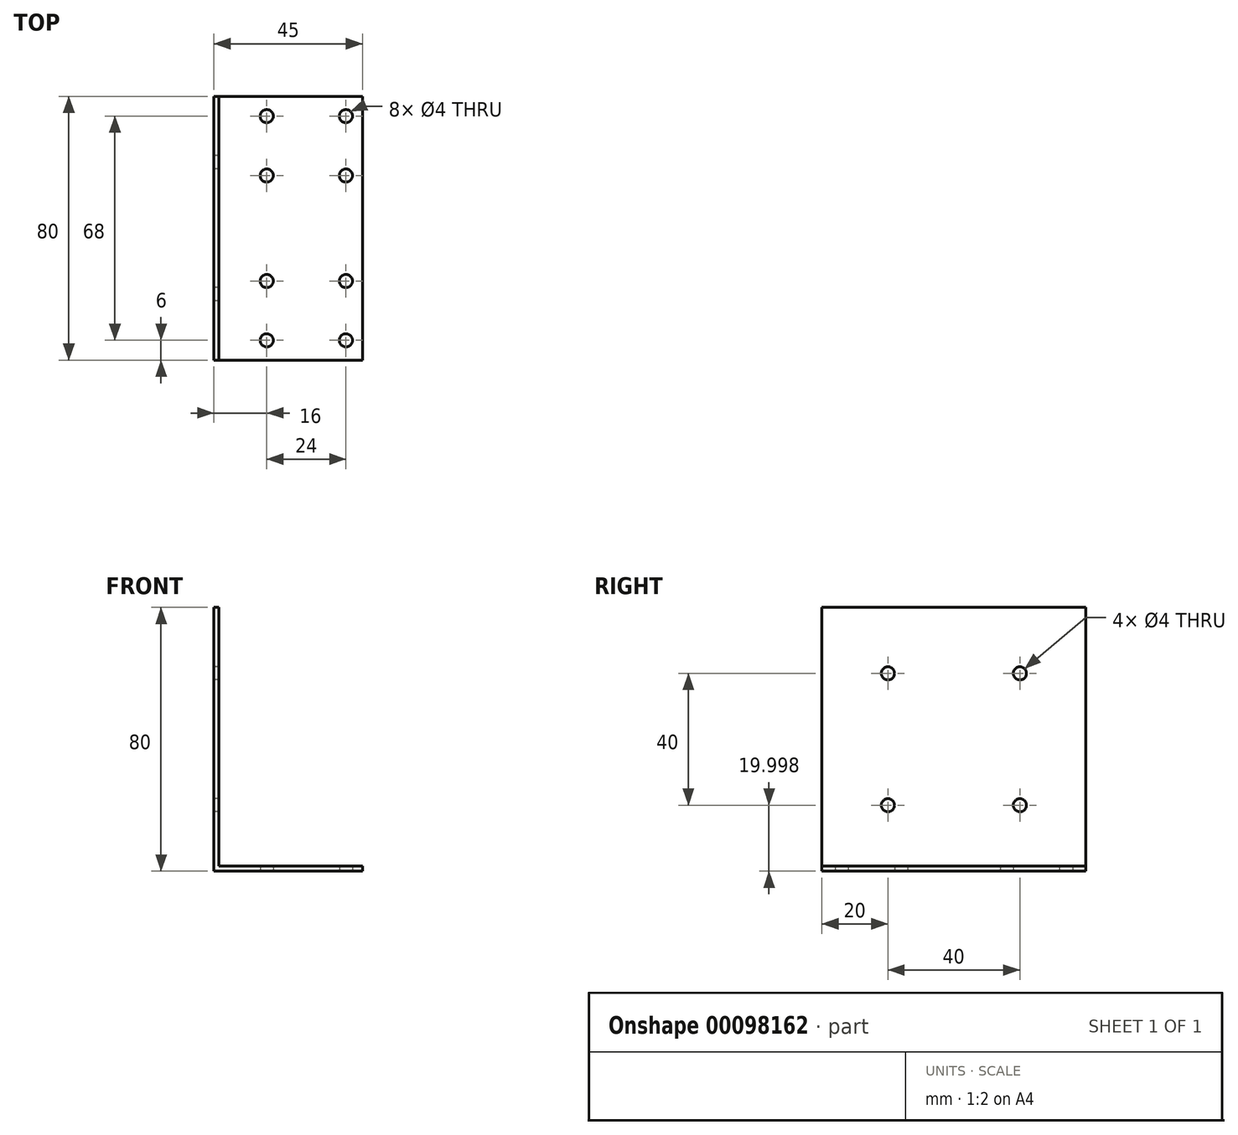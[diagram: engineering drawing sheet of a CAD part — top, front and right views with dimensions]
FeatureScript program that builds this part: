
annotation { "Feature Type Name" : "Feature", "Feature Type Description" : "" }
export const myFeature = defineFeature(function(context is Context, id is Id, definition is map)
    precondition{}
    {
        {
            var Q0;
            Q0=qCreatedBy(makeId("Front.planeOp"),FACE);
            var sketch = newSketch(context, id + "F0", { "sketchPlane" : qUnion([Q0])});
            skLineSegment(sketch, "E0", {"start": v(-85.27, 112.48) * mm, "end": v(-85.27, 32.48) * mm});
            skLineSegment(sketch, "E1", {"start": v(-85.27, 32.48) * mm, "end": v(-40.27, 32.48) * mm});
            skLineSegment(sketch, "E2", {"start": v(-40.27, 32.48) * mm, "end": v(-40.27, 33.98) * mm});
            skLineSegment(sketch, "E3", {"start": v(-40.27, 33.98) * mm, "end": v(-83.77, 33.98) * mm});
            skLineSegment(sketch, "E4", {"start": v(-83.77, 33.98) * mm, "end": v(-83.77, 112.48) * mm});
            skLineSegment(sketch, "E5", {"start": v(-83.77, 112.48) * mm, "end": v(-85.27, 112.48) * mm});
            skSolve(sketch);
        }
        {
            var Q0;
            Q0=makeQuery(id+"F0.imprint","IMPRINT",FACE,{"disambiguationData":[TD([[makeQuery(id+"F0.imprint","IMPRINT",EDGE,{"derivedFrom":sQuery(id+"F0.wireOp",EDGE,"E0")}),1.0]])]});
            extrude(context, id + "F1", {"entities" : qUnion([Q0]), "depth" : 80 * mm});
        }
        {
            var Q0;
            Q0=makeQuery(id+"F1.opExtrude","SWEPT_FACE",FACE,{"disambiguationData":[OSD([sQuery(id+"F0.wireOp",EDGE,"E1")])]});
            var sketch = newSketch(context, id + "F2", { "sketchPlane" : qUnion([Q0])});
            skPoint(sketch, "E6.startSnap0", {"position": v(-62.77, 80) * mm});
            skLineSegment(sketch, "E7", {"start": v(-94.66, 40) * mm, "end": v(-37.45, 40) * mm, "construction": true});
            skPoint(sketch, "E7.startSnap0", {"position": v(-85.27, 40) * mm});
            skLineSegment(sketch, "E8", {"start": v(-91.67, 65) * mm, "end": v(-32.26, 65) * mm, "construction": true});
            skPoint(sketch, "E9.MirrorP", {"position": v(-45.27, 74) * mm});
            skLineSegment(sketch, "E10", {"start": v(-57.27, -6.03) * mm, "end": v(-57.27, 93.49) * mm, "construction": true});
            skPoint(sketch, "E11.MirrorP", {"position": v(-45.27, 56) * mm});
            skPoint(sketch, "E12.MirrorP", {"position": v(-69.27, 56) * mm});
            skPoint(sketch, "E13.MirrorP", {"position": v(-69.27, 74) * mm});
            skPoint(sketch, "E14.MirrorP", {"position": v(-69.27, 24) * mm});
            skPoint(sketch, "E15.MirrorP", {"position": v(-69.27, 6) * mm});
            skPoint(sketch, "E16.MirrorP", {"position": v(-45.27, 6) * mm});
            skPoint(sketch, "E17.MirrorP", {"position": v(-45.27, 24) * mm});
            skSolve(sketch);
        }
        {
            var Q0;
            Q0=sQuery(id+"F2.wireOp",VERTEX,"E9.MirrorP");
            var Q1;
            Q1=sQuery(id+"F2.wireOp",VERTEX,"E13.MirrorP");
            var Q2;
            Q2=sQuery(id+"F2.wireOp",VERTEX,"E12.MirrorP");
            var Q3;
            Q3=sQuery(id+"F2.wireOp",VERTEX,"E11.MirrorP");
            var Q4;
            Q4=sQuery(id+"F2.wireOp",VERTEX,"E17.MirrorP");
            var Q5;
            Q5=sQuery(id+"F2.wireOp",VERTEX,"E16.MirrorP");
            var Q6;
            Q6=sQuery(id+"F2.wireOp",VERTEX,"E15.MirrorP");
            var Q7;
            Q7=sQuery(id+"F2.wireOp",VERTEX,"E14.MirrorP");
            var Q8;
            Q8=makeQuery(id+"F1.opExtrude","SWEPT_BODY",BODY,{"disambiguationData":[OSD([sQuery(id+"F0.wireOp",EDGE,"E0"),sQuery(id+"F0.wireOp",EDGE,"E1"),sQuery(id+"F0.wireOp",EDGE,"E2"),sQuery(id+"F0.wireOp",EDGE,"E3"),sQuery(id+"F0.wireOp",EDGE,"E4"),sQuery(id+"F0.wireOp",EDGE,"E5")])]});
            hole(context, id + "F3", {"style" : HoleStyle.SIMPLE, "endStyle" : HoleEndStyle.THROUGH, "holeDiameter" : 4 * mm, "locations" : qUnion([Q0, Q1, Q2, Q3, Q4, Q5, Q6, Q7]), "scope" : qUnion([Q8]), "isTappedThrough" : true});
        }
        {
            var Q0;
            Q0=makeQuery(id+"F1.opExtrude","SWEPT_FACE",FACE,{"disambiguationData":[OSD([sQuery(id+"F0.wireOp",EDGE,"E0")])]});
            var sketch = newSketch(context, id + "F4", { "sketchPlane" : qUnion([Q0])});
            skPoint(sketch, "E18", {"position": v(20, 92.48) * mm});
            skPoint(sketch, "E19", {"position": v(20, 52.48) * mm});
            skPoint(sketch, "E20", {"position": v(60, 52.48) * mm});
            skPoint(sketch, "E21", {"position": v(60, 92.48) * mm});
            skSolve(sketch);
        }
        {
            var Q0;
            Q0=sQuery(id+"F4.wireOp",VERTEX,"E19");
            var Q1;
            Q1=sQuery(id+"F4.wireOp",VERTEX,"E20");
            var Q2;
            Q2=sQuery(id+"F4.wireOp",VERTEX,"E21");
            var Q3;
            Q3=sQuery(id+"F4.wireOp",VERTEX,"E18");
            var Q4;
            Q4=makeQuery(id+"F1.opExtrude","SWEPT_BODY",BODY,{"disambiguationData":[OSD([sQuery(id+"F0.wireOp",EDGE,"E0"),sQuery(id+"F0.wireOp",EDGE,"E1"),sQuery(id+"F0.wireOp",EDGE,"E2"),sQuery(id+"F0.wireOp",EDGE,"E3"),sQuery(id+"F0.wireOp",EDGE,"E4"),sQuery(id+"F0.wireOp",EDGE,"E5")])]});
            hole(context, id + "F5", {"style" : HoleStyle.SIMPLE, "endStyle" : HoleEndStyle.THROUGH, "holeDiameter" : 4 * mm, "locations" : qUnion([Q0, Q1, Q2, Q3]), "scope" : qUnion([Q4]), "isTappedThrough" : true});
        }
    });
